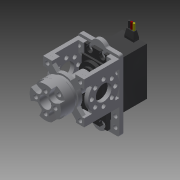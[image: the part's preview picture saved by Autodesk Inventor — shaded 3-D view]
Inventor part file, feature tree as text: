
AUTODESK INVENTOR PART (.ipt)
format: ipt  version: 2013 (Build 170138000, 138)  size: 769,536 bytes
history: native  units: in
note: dims shown in document units (in); Inventor stores cm internally (conversion verified against a paired STEP export)
features: extrude x23, sketch x23, other x11, projected_geometry x10, fillet x3, mirror x2, plane x1, pattern_circular x1
ambient origin geometry x8: Origin, YZ Plane, XZ Plane, XY Plane, X Axis, Y Axis, Z Axis, Center Point
feature tree (74):
  other  "Servo"
  extrude  "Extrusion1"  Depth=1.525in
  extrude  "Extrusion2"  Depth=0.025in
  extrude  "Extrusion3"  Depth=0.17in
  fillet  "Fillet1"  Radius=0.11in
  plane  "Work Plane1"
  extrude  "Extrusion4"  Depth=0.391in
  fillet  "Fillet2"  Radius=0.07in
  mirror  "Mirror1"
  extrude  "Extrusion5"  [1 undecoded]
  extrude  "Extrusion6"  Depth=0.28in
  extrude  "Extrusion7"  Depth=0.165in
  extrude  "Extrusion8"  Depth=0.1in TaperAngle=0.0deg
  extrude  "Extrusion9"  Depth=0.3in
  extrude  "Extrusion10"  Depth=0.01in
  fillet  "Fillet3"  Radius=0.0625in
  extrude  "Extrusion11"  Depth=0.0625in
  extrude  "Extrusion12"  Depth=0.0625in
  extrude  "Extrusion13"  Depth=0.2in TaperAngle=0.0deg
  extrude  "Extrusion14"  Depth=0.04in
  extrude  "Extrusion15"  Depth=0.136in
  extrude  "Extrusion16"  Depth=0.125in
  mirror  "Mirror2"
  extrude  "Extrusion18"  Depth=0.25in
  extrude  "Extrusion19"  Depth=0.2165in
  extrude  "Extrusion20"  Depth=0.1325in
  extrude  "Extrusion21"  Depth=0.3125in
  extrude  "Extrusion22"  Depth=0.125in TaperAngle=0.0deg
  extrude  "Extrusion23"  Depth=0.125in
  extrude  "Extrusion24"  Depth=0.083in
  pattern_circular  "Circular Pattern1"  [2 undecoded]
  sketch  "Sketch1"  dims[d0=0.782in d1=1.525in]
  sketch  "Sketch2"  dims[d2=1.305in d3=0.0in d4=0.025in]
  sketch  "Sketch3"  dims[d5=0.025in d6=0.17in d7=0.11in d8=0.0in]
  sketch  "Sketch4"  dims[d9=0.508in d11=0.391in d12=0.07in d13=0.0in]
  sketch  "Sketch5"  dims[d14=0.366in d15=-0.16in]
  sketch  "Sketch6"  dims[d16=0.737in d18=0.28in]
  sketch  "Sketch7"  dims[d19=0.1in d20=0.21in d21=0.165in]
  other  "Red wire"
  sketch  "Sketch8"  dims[d22=0.165in d23=0.1in d24=0.0in]
  sketch  "Sketch9"  dims[d25=0.01in d26=0.3in]
  other  "Yellow Wire"
  sketch  "Sketch10"  dims[d27=0.17in d28=0.01in d29=0.0625in d30=0.0in]
  other  "BaseStructure"
  sketch  "Sketch11"  dims[d31=0.2in d32=-0.0687in d33=0.0625in]
  other  "ServoOutput"
  sketch  "Sketch12"  dims[d34=0.2in d35=0.0in d36=0.0625in]
  other  "SideStructure"
  sketch  "Sketch13"  dims[d37=0.04in d38=0.2in d39=0.0in]
  sketch  "Sketch14"  dims[d40=0.0625in d41=0.04in]
  projected_geometry  "Projected Loop1"
  projected_geometry  "Projected Loop2"
  sketch  "Sketch16"  dims[d42=0.2in d43=0.0in d44=0.136in]
  sketch  "Sketch17"  dims[d47=2.25in d48=0.125in]
  other  "Pattern of SideStructure:1"
  other  "SideStructureMirror"
  sketch  "Sketch18"  dims[d49=0.25in d50=0.25in]
  projected_geometry  "Projected Loop3"
  projected_geometry  "Projected Loop4"
  projected_geometry  "Projected Loop5"
  projected_geometry  "Projected Loop6"
  projected_geometry  "Projected Loop7"
  other  "BearingStructure"
  sketch  "Sketch19"  dims[d51=0.125in d52=0.2165in]
  sketch  "Sketch20"  dims[d53=0.1325in d54=0.1325in]
  other  "HubShaft"
  sketch  "Sketch21"  dims[d55=1.3125in d56=0.3125in]
  sketch  "Sketch22"  dims[d57=0.435in d58=0.125in d59=0.0in]
  sketch  "Sketch23"  dims[d60=0.0625in d61=0.125in]
  other  "HubAdapter"
  sketch  "Sketch24"  dims[d62=0.0625in d63=0.0in d66=0.083in d67=0.083in d68=0.125in d69=0.125in d70=0.125in d71=0.0in d72=0.125in d73=0.75in d74=0.0in d75=0.125in d76=0.0in d80=1.0in d82=0.125in d83=0.0in d84=0.5in d85=0.75in d86=0.136in d87=3.1496in d89=360.0deg d91=0.125in d92=0.0in d93=0.95in d94=45.0deg d96=0.26in d97=0.13in d100=45.0deg d101=0.13in d102=0.26in d103=0.125in d104=0.0in d105=0.845in d106=0.072in d107=0.0in d108=0.5in d109=0.8575in d110=0.0in d111=1.0in d112=0.75in d113=0.136in d114=3.1496in d116=360.0deg d118=0.2in d119=0.0in d120=0.3in d121=0.2in d122=0.0in d123=0.375in d124=0.625in d125=0.136in d126=1.5748in d128=360.0deg d130=0.25in d131=0.0in d133=0.1374in d134=0.1374in d135=0.168in d136=0.0in d137=1.5748in d138=360.0deg]
  projected_geometry  "Project Cut Edges1"
  projected_geometry  "Project Cut Edges2"
  projected_geometry  "Project Cut Edges3"
note: 3 required parameter values undecoded (feature->parameter linkage not recoverable at this tier; creation-order binding heuristic only, values carry confidence <= 0.55)
